# Revit family: Bench_Curved_Noble
name_source: partatom
category: Specialty Equipment
revit_build: Autodesk Revit 2016 (Build: 20150714_1515(x64)
units: mm (PartAtom-declared; Revit-internal decimal feet)

## family parameters
Cut with Voids When Loaded = No
Host = Face
OmniClass Number = 23.45.55.21
OmniClass Title = Drains (Wastes)
Part Type = Normal
Room Calculation Point = No
Round Connector Dimension = Use Diameter
Shared = No

## types (1)
- Curved #406
    Assembly Code = D2030300
    Base = Polymer coated Expanded Polystyrene
    Building Codes = http://www.noblecompany.com
    Default Elevation = 0"
    Height = 20"
    Installation-Fabrication = http://www.noblecompany.com
    Length = 32 1/2"
    Manufacturer = Noble Company
    Manufacturer Fax = 231-799-8850
    Product Data = http://www.noblecompany.com
    Product Properties = http://www.noblecompany.com
    Radius = 15 1/2"
    Triangle = Yes
    URL = www.noblecompany.com
    Width = 32 1/2"

## geometry (parser evidence)
native form markers: Sweep x5
no freeform markers — native parametric forms only
